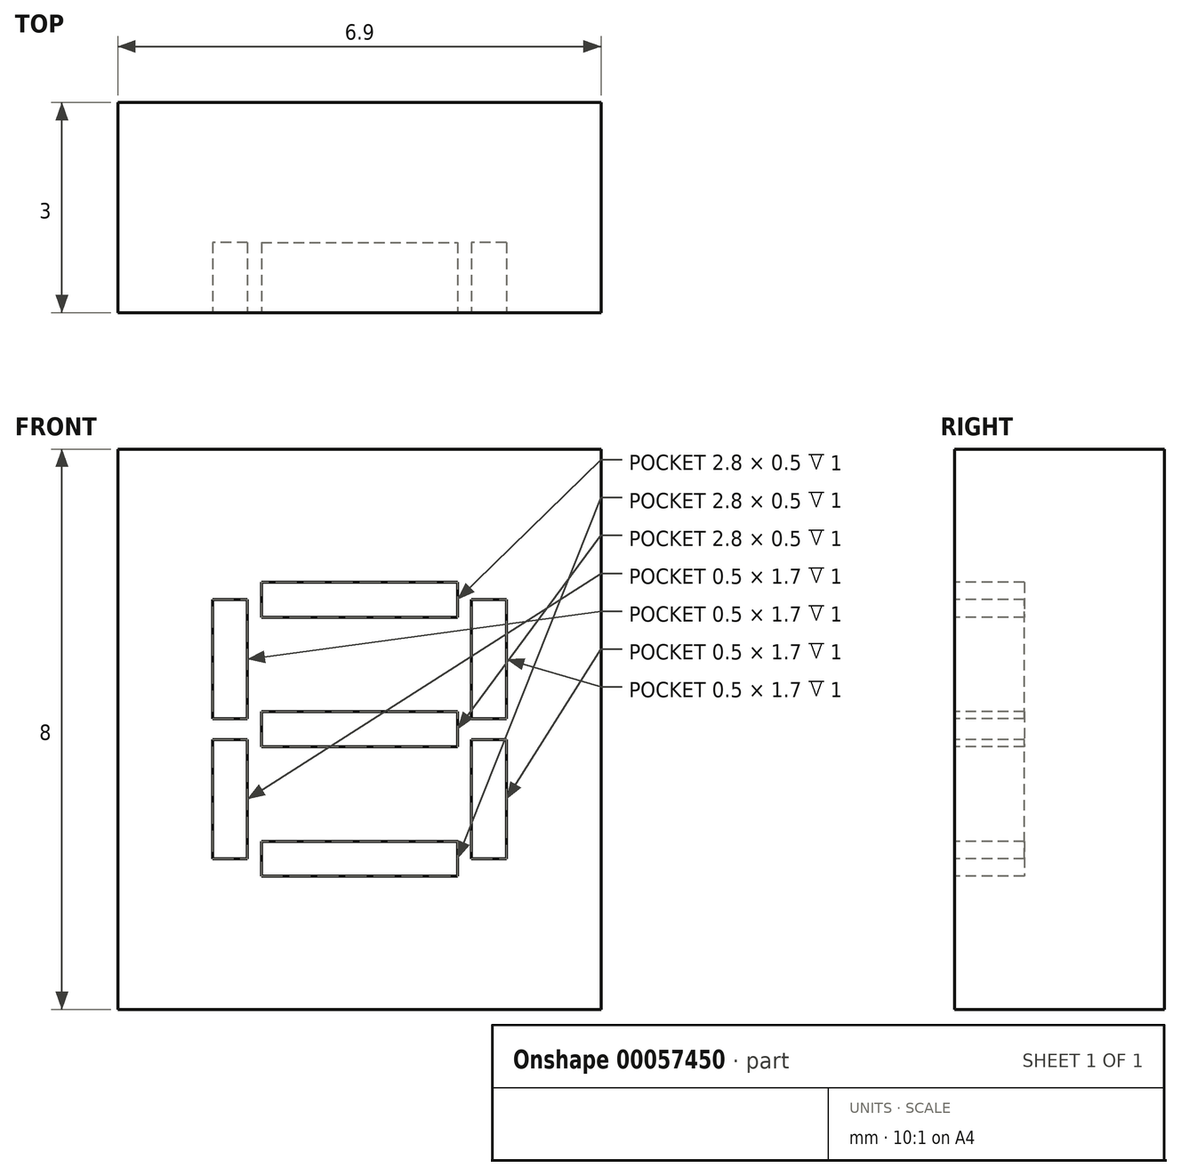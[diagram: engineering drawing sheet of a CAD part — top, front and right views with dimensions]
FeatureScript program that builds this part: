
annotation { "Feature Type Name" : "Feature", "Feature Type Description" : "" }
export const myFeature = defineFeature(function(context is Context, id is Id, definition is map)
    precondition{}
    {
        {
            var Q0;
            Q0=qCreatedBy(makeId("Front.planeOp"),FACE);
            var sketch = newSketch(context, id + "F0", { "sketchPlane" : qUnion([Q0])});
            skLineSegment(sketch, "E0.bottom", {"start": v(0, 0) * mm, "end": v(6.9, 0) * mm});
            skLineSegment(sketch, "E0.top", {"start": v(0, -8) * mm, "end": v(6.9, -8) * mm});
            skLineSegment(sketch, "E0.left", {"start": v(0, 0) * mm, "end": v(0, -8) * mm});
            skLineSegment(sketch, "E0.right", {"start": v(6.9, 0) * mm, "end": v(6.9, -8) * mm});
            skSolve(sketch);
        }
        {
            var Q0;
            Q0=makeQuery(id+"F0.imprint","IMPRINT",FACE,{"disambiguationData":[TD([[makeQuery(id+"F0.imprint","IMPRINT",EDGE,{"derivedFrom":sQuery(id+"F0.wireOp",EDGE,"E0.bottom")}),-1.0]])]});
            extrude(context, id + "F1", {"entities" : qUnion([Q0]), "depth" : 3 * mm});
        }
        {
            var Q0;
            Q0=makeQuery(id+"F1.opExtrude","CAP_FACE",FACE,{"disambiguationData":[OSD([sQuery(id+"F0.wireOp",EDGE,"E0.bottom"),sQuery(id+"F0.wireOp",EDGE,"E0.top"),sQuery(id+"F0.wireOp",EDGE,"E0.left"),sQuery(id+"F0.wireOp",EDGE,"E0.right")])],"isStart":false});
            var sketch = newSketch(context, id + "F2", { "sketchPlane" : qUnion([Q0])});
            skLineSegment(sketch, "E1.bottom", {"start": v(2.05, -1.9) * mm, "end": v(4.85, -1.9) * mm});
            skLineSegment(sketch, "E1.top", {"start": v(2.05, -2.4) * mm, "end": v(4.85, -2.4) * mm});
            skLineSegment(sketch, "E1.left", {"start": v(2.05, -1.9) * mm, "end": v(2.05, -2.4) * mm});
            skLineSegment(sketch, "E1.right", {"start": v(4.85, -1.9) * mm, "end": v(4.85, -2.4) * mm});
            skLineSegment(sketch, "E2.right", {"start": v(4.85, -5.6) * mm, "end": v(4.85, -6.1) * mm});
            skLineSegment(sketch, "E2.top", {"start": v(2.05, -6.1) * mm, "end": v(4.85, -6.1) * mm});
            skLineSegment(sketch, "E2.bottom", {"start": v(2.05, -5.6) * mm, "end": v(4.85, -5.6) * mm});
            skLineSegment(sketch, "E2.left", {"start": v(2.05, -5.6) * mm, "end": v(2.05, -6.1) * mm});
            skLineSegment(sketch, "E3.bottom", {"start": v(2.05, -3.75) * mm, "end": v(4.85, -3.75) * mm});
            skLineSegment(sketch, "E3.top", {"start": v(2.05, -4.25) * mm, "end": v(4.85, -4.25) * mm});
            skLineSegment(sketch, "E3.right", {"start": v(4.85, -3.75) * mm, "end": v(4.85, -4.25) * mm});
            skLineSegment(sketch, "E3.left", {"start": v(2.05, -3.75) * mm, "end": v(2.05, -4.25) * mm});
            skLineSegment(sketch, "E4.bottom", {"start": v(1.85, -5.85) * mm, "end": v(1.35, -5.85) * mm});
            skLineSegment(sketch, "E4.top", {"start": v(1.85, -4.15) * mm, "end": v(1.35, -4.15) * mm});
            skLineSegment(sketch, "E4.left", {"start": v(1.85, -5.85) * mm, "end": v(1.85, -4.15) * mm});
            skLineSegment(sketch, "E4.right", {"start": v(1.35, -5.85) * mm, "end": v(1.35, -4.15) * mm});
            skLineSegment(sketch, "E5.right", {"start": v(1.35, -3.85) * mm, "end": v(1.35, -2.15) * mm});
            skLineSegment(sketch, "E5.left", {"start": v(1.85, -3.85) * mm, "end": v(1.85, -2.15) * mm});
            skLineSegment(sketch, "E5.top", {"start": v(1.85, -2.15) * mm, "end": v(1.35, -2.15) * mm});
            skLineSegment(sketch, "E5.bottom", {"start": v(1.85, -3.85) * mm, "end": v(1.35, -3.85) * mm});
            skLineSegment(sketch, "E6.right", {"start": v(5.05, -5.85) * mm, "end": v(5.05, -4.15) * mm});
            skLineSegment(sketch, "E6.left", {"start": v(5.55, -5.85) * mm, "end": v(5.55, -4.15) * mm});
            skLineSegment(sketch, "E6.top", {"start": v(5.55, -4.15) * mm, "end": v(5.05, -4.15) * mm});
            skLineSegment(sketch, "E7.left", {"start": v(5.55, -3.85) * mm, "end": v(5.55, -2.15) * mm});
            skLineSegment(sketch, "E7.bottom", {"start": v(5.55, -3.85) * mm, "end": v(5.05, -3.85) * mm});
            skLineSegment(sketch, "E7.right", {"start": v(5.05, -3.85) * mm, "end": v(5.05, -2.15) * mm});
            skLineSegment(sketch, "E7.top", {"start": v(5.55, -2.15) * mm, "end": v(5.05, -2.15) * mm});
            skLineSegment(sketch, "E6.bottom", {"start": v(5.55, -5.85) * mm, "end": v(5.05, -5.85) * mm});
            skSolve(sketch);
        }
        {
            var Q0;
            Q0 = qSketchRegion(id + "F2", true);
            extrude(context, id + "F3", {"entities" : qUnion([Q0]), "operationType" : NewBodyOperationType.REMOVE, "oppositeDirection" : true, "depth" : 1 * mm});
        }
    });
